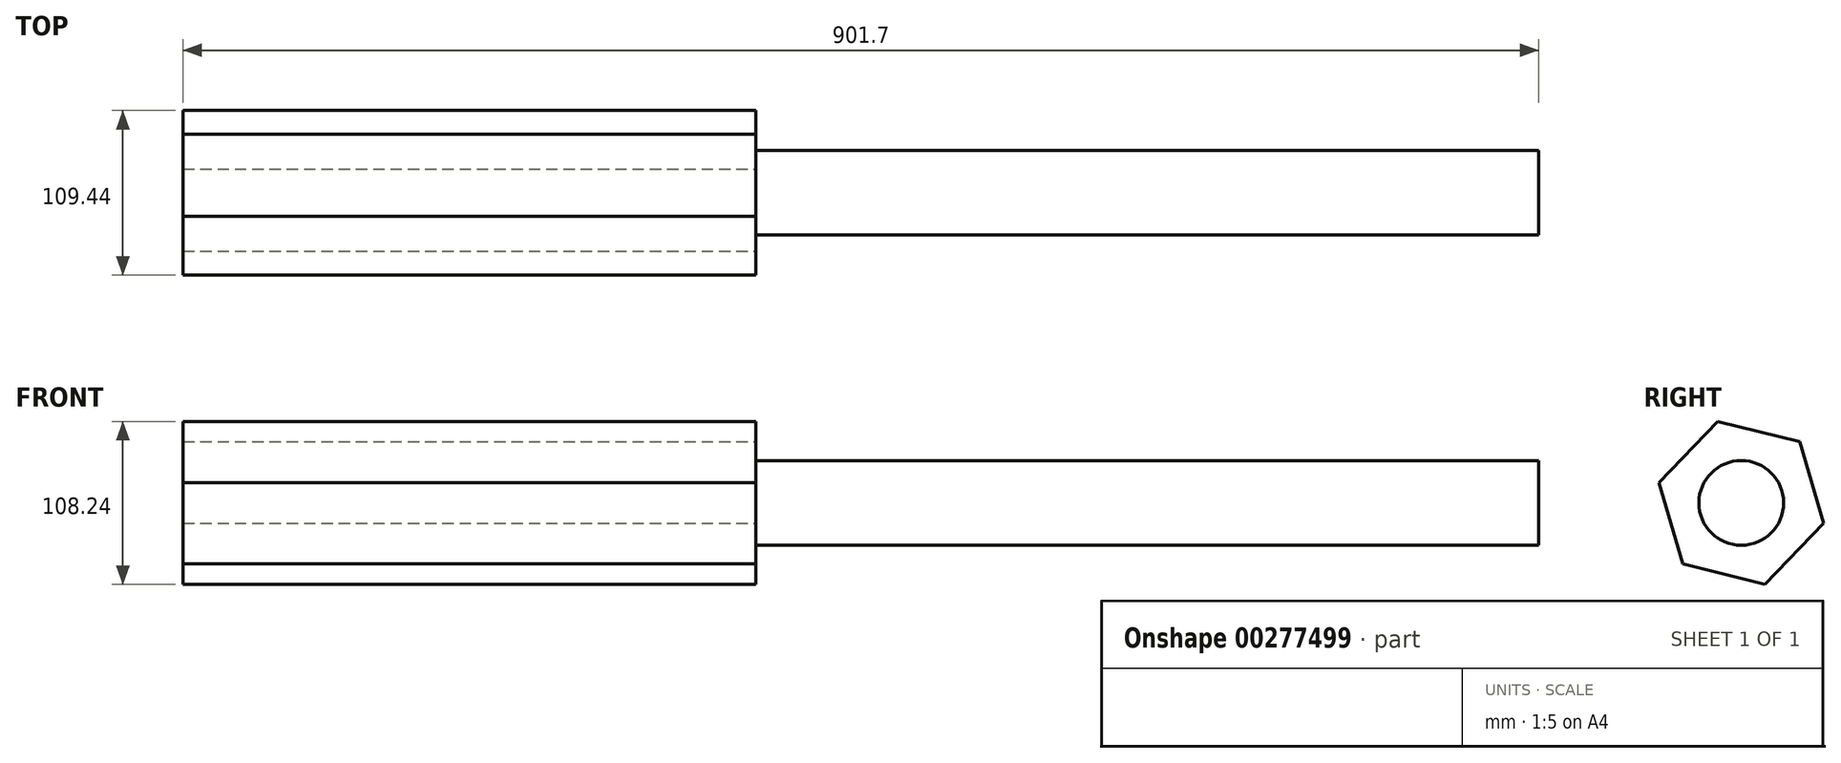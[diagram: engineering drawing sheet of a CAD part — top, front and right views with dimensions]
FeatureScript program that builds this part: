
annotation { "Feature Type Name" : "Feature", "Feature Type Description" : "" }
export const myFeature = defineFeature(function(context is Context, id is Id, definition is map)
    precondition{}
    {
        {
            var Q0;
            Q0=qCreatedBy(makeId("Right.planeOp"),FACE);
            var sketch = newSketch(context, id + "F0", { "sketchPlane" : qUnion([Q0])});
            skCircle(sketch, "E0", {"center": v(0, 0) * mm, "radius": 28.2 * mm});
            skSolve(sketch);
        }
        {
            var Q0;
            Q0 = qSketchRegion(id + "F0", true);
            extrude(context, id + "F1", {"entities" : qUnion([Q0]), "endBound" : BoundingType.SYMMETRIC, "depth" : 711.2 * mm});
        }
        {
            var Q0;
            Q0=makeQuery(id+"F1.opExtrude","CAP_FACE",FACE,{"disambiguationData":[OSD([sQuery(id+"F0.wireOp",EDGE,"E0")])],"isStart":true});
            var sketch = newSketch(context, id + "F2", { "sketchPlane" : qUnion([Q0])});
            skCircle(sketch, "E1.cCircle", {"center": v(0, 0) * mm, "radius": 48.8 * mm, "construction": true});
            skLineSegment(sketch, "E1.0", {"start": v(15.7, 54.12) * mm, "end": v(54.72, 13.46) * mm});
            skLineSegment(sketch, "E1.1", {"start": v(54.72, 13.46) * mm, "end": v(39.01, -40.66) * mm});
            skLineSegment(sketch, "E1.2", {"start": v(39.01, -40.66) * mm, "end": v(-15.7, -54.12) * mm});
            skLineSegment(sketch, "E1.3", {"start": v(-15.7, -54.12) * mm, "end": v(-54.72, -13.46) * mm});
            skLineSegment(sketch, "E1.4", {"start": v(-54.72, -13.46) * mm, "end": v(-39.01, 40.66) * mm});
            skLineSegment(sketch, "E1.5", {"start": v(-39.01, 40.66) * mm, "end": v(15.7, 54.12) * mm});
            skPoint(sketch, "E1.0.midPoint", {"position": v(35.21, 33.79) * mm});
            skSolve(sketch);
        }
        {
            var Q0;
            Q0 = qSketchRegion(id + "F2", true);
            extrude(context, id + "F3", {"entities" : qUnion([Q0]), "operationType" : NewBodyOperationType.ADD, "endBound" : BoundingType.SYMMETRIC, "depth" : 381 * mm});
        }
    });
